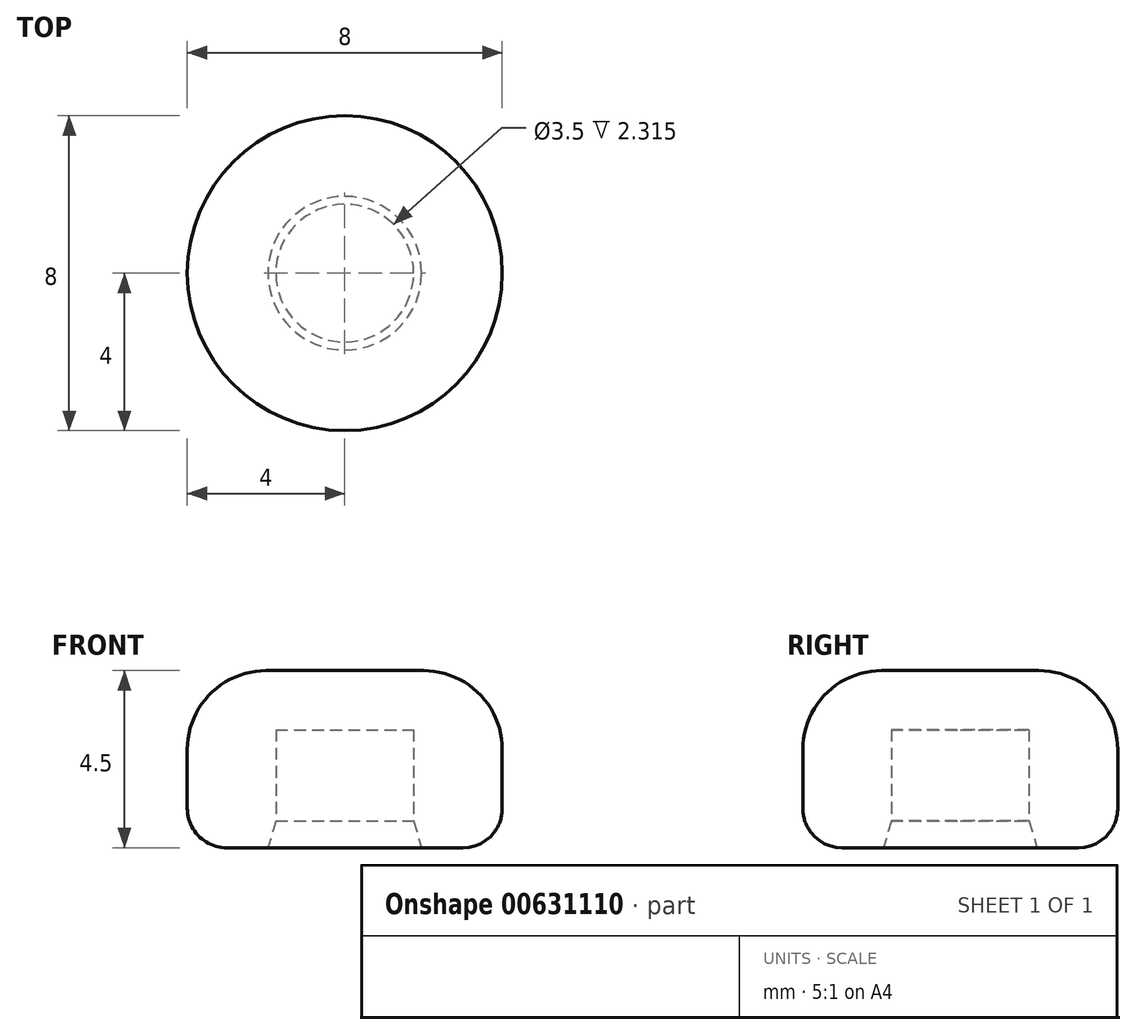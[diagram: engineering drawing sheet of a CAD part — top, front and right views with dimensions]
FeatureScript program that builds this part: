
annotation { "Feature Type Name" : "Feature", "Feature Type Description" : "" }
export const myFeature = defineFeature(function(context is Context, id is Id, definition is map)
    precondition{}
    {
        {
            var Q0;
            Q0=qCreatedBy(makeId("Front.planeOp"),FACE);
            var sketch = newSketch(context, id + "F0", { "sketchPlane" : qUnion([Q0])});
            skLineSegment(sketch, "E0", {"start": v(0, 0) * mm, "end": v(0, 289.91) * mm, "construction": true});
            skLineSegment(sketch, "E1", {"start": v(4, 1) * mm, "end": v(4, 2.5) * mm});
            skLineSegment(sketch, "E2", {"start": v(2, 4.5) * mm, "end": v(0, 4.5) * mm});
            skLineSegment(sketch, "E3", {"start": v(0, 4.5) * mm, "end": v(0, 3) * mm});
            skLineSegment(sketch, "E4", {"start": v(0, 3) * mm, "end": v(1.75, 3) * mm});
            skLineSegment(sketch, "E5", {"start": v(1.75, 3) * mm, "end": v(1.75, 0.69) * mm});
            skPoint(sketch, "E6.visualSharp", {"position": v(4, 4.5) * mm});
            skArc(sketch, "E6.filletArc", {"start": v(4, 2.5) * mm, "mid": v(3.41, 3.91) * mm, "end": v(2, 4.5) * mm});
            skPoint(sketch, "E7.visualSharp", {"position": v(4, 0) * mm});
            skLineSegment(sketch, "E8", {"start": v(1.75, 0) * mm, "end": v(1.75, 0) * mm});
            skPoint(sketch, "E9.start.orphan", {"position": v(1.75, 0) * mm});
            skLineSegment(sketch, "E10", {"start": v(1.95, 0) * mm, "end": v(3, 0) * mm});
            skArc(sketch, "E11.filletArc", {"start": v(3, 0) * mm, "mid": v(3.7, 0.3) * mm, "end": v(4, 1) * mm});
            skLineSegment(sketch, "E12", {"start": v(1.75, 0.69) * mm, "end": v(1.95, 0) * mm});
            skSolve(sketch);
        }
        {
            var Q0;
            Q0 = qSketchRegion(id + "F0", true);
            var Q1;
            Q1=sQuery(id+"F0.wireOp",EDGE,"E0");
            revolve(context, id + "F1", {"entities" : qUnion([Q0]), "axis" : qUnion([Q1]), "revolveType" : RevolveType.FULL});
        }
    });
